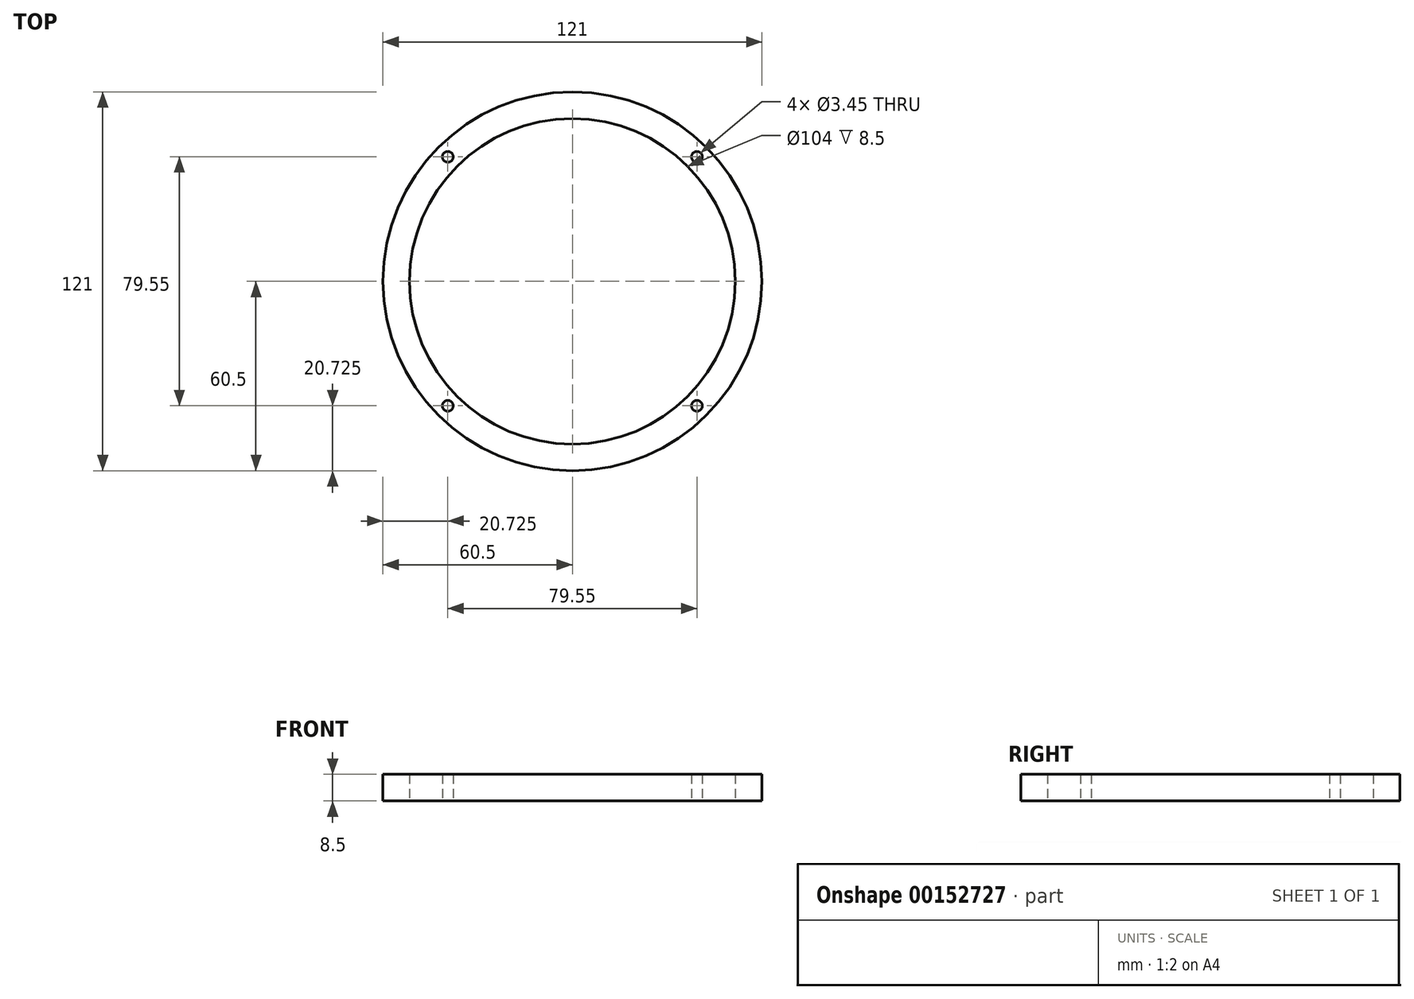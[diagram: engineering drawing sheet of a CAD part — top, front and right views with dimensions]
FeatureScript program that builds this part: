
annotation { "Feature Type Name" : "Feature", "Feature Type Description" : "" }
export const myFeature = defineFeature(function(context is Context, id is Id, definition is map)
    precondition{}
    {
        {
            var Q0;
            Q0=qCreatedBy(makeId("Top.planeOp"),FACE);
            var sketch = newSketch(context, id + "F0", { "sketchPlane" : qUnion([Q0])});
            skCircle(sketch, "E0", {"center": v(0, 0) * mm, "radius": 52 * mm});
            skCircle(sketch, "E1", {"center": v(0, 0) * mm, "radius": 60.5 * mm});
            skCircle(sketch, "E2", {"center": v(-39.77, 39.77) * mm, "radius": 4.25 * mm, "construction": true});
            skLineSegment(sketch, "E3.bottom", {"start": v(-39.77, 39.77) * mm, "end": v(39.77, 39.77) * mm, "construction": true});
            skLineSegment(sketch, "E3.top", {"start": v(-39.77, -39.77) * mm, "end": v(39.77, -39.77) * mm, "construction": true});
            skLineSegment(sketch, "E3.left", {"start": v(-39.77, 39.77) * mm, "end": v(-39.77, -39.77) * mm, "construction": true});
            skLineSegment(sketch, "E3.right", {"start": v(39.77, 39.77) * mm, "end": v(39.77, -39.77) * mm, "construction": true});
            skCircle(sketch, "E4", {"center": v(-39.77, 39.77) * mm, "radius": 1.73 * mm});
            skCircle(sketch, "E5", {"center": v(-39.77, -39.77) * mm, "radius": 1.73 * mm});
            skCircle(sketch, "E6", {"center": v(39.77, -39.77) * mm, "radius": 1.73 * mm});
            skCircle(sketch, "E7", {"center": v(39.77, 39.77) * mm, "radius": 1.73 * mm});
            skSolve(sketch);
        }
        {
            var Q0;
            Q0=qSketchRegion(id+"F0",true);
            extrude(context, id + "F1", {"entities" : qUnion([Q0]), "depth" : 8.5 * mm});
        }
    });
